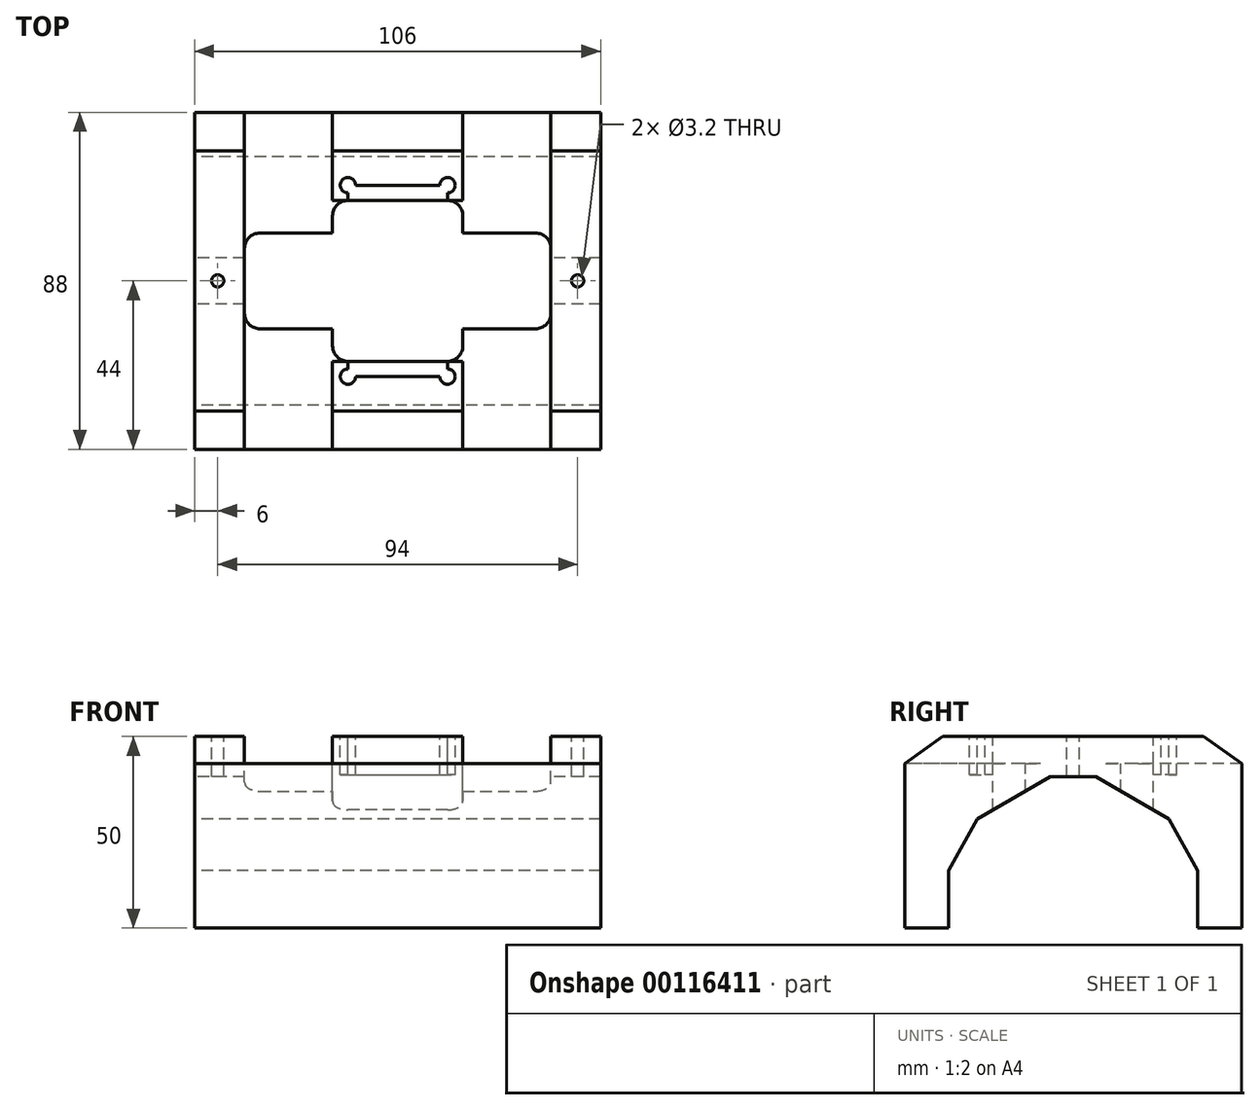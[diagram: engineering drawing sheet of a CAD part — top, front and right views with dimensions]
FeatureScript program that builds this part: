
annotation { "Feature Type Name" : "Feature", "Feature Type Description" : "" }
export const myFeature = defineFeature(function(context is Context, id is Id, definition is map)
    precondition{}
    {
        {
            var Q0;
            Q0=qCreatedBy(makeId("Right.planeOp"),FACE);
            var sketch = newSketch(context, id + "F0", { "sketchPlane" : qUnion([Q0])});
            skLineSegment(sketch, "E0.bottom", {"start": v(-44, 25) * mm, "end": v(44, 25) * mm});
            skLineSegment(sketch, "E0.top", {"start": v(-44, -25) * mm, "end": v(-32.5, -25) * mm});
            skLineSegment(sketch, "E0.left", {"start": v(-44, 25) * mm, "end": v(-44, -25) * mm});
            skLineSegment(sketch, "E0.right", {"start": v(44, 25) * mm, "end": v(44, -25) * mm});
            skPoint(sketch, "E0.middle", {"position": v(0, 0) * mm});
            skLineSegment(sketch, "E1.0", {"start": v(-44, 14.5) * mm, "end": v(44, 14.5) * mm, "construction": true});
            skLineSegment(sketch, "E2.0", {"start": v(-44, 3.5) * mm, "end": v(44, 3.5) * mm, "construction": true});
            skLineSegment(sketch, "E3.0", {"start": v(-44, -10) * mm, "end": v(44, -10) * mm, "construction": true});
            skLineSegment(sketch, "E4", {"start": v(0, -34.88) * mm, "end": v(0, 37.1) * mm, "construction": true});
            skPoint(sketch, "E4.startSnap0", {"position": v(0, -25) * mm});
            skLineSegment(sketch, "E5.0", {"start": v(6, -34.88) * mm, "end": v(6, 37.1) * mm, "construction": true});
            skLineSegment(sketch, "E6.0", {"start": v(25, -34.88) * mm, "end": v(25, 37.1) * mm, "construction": true});
            skLineSegment(sketch, "E7.0", {"start": v(32.5, -34.88) * mm, "end": v(32.5, 37.1) * mm, "construction": true});
            skLineSegment(sketch, "E8", {"start": v(32.5, -10) * mm, "end": v(25, 3.5) * mm});
            skLineSegment(sketch, "E9", {"start": v(25, 3.5) * mm, "end": v(6, 14.5) * mm});
            skLineSegment(sketch, "E10", {"start": v(6, 14.5) * mm, "end": v(0, 14.5) * mm});
            skLineSegment(sketch, "E11", {"start": v(32.5, -10) * mm, "end": v(32.5, -25) * mm});
            skLineSegment(sketch, "E12.MirrorCS", {"start": v(-32.5, -10) * mm, "end": v(-32.5, -25) * mm});
            skLineSegment(sketch, "E13.MirrorCS", {"start": v(-6, 14.5) * mm, "end": v(0, 14.5) * mm});
            skLineSegment(sketch, "E14.MirrorCS", {"start": v(-25, 3.5) * mm, "end": v(-6, 14.5) * mm});
            skLineSegment(sketch, "E15.MirrorCS", {"start": v(-32.5, -10) * mm, "end": v(-25, 3.5) * mm});
            skLineSegment(sketch, "E16.trimOffspring", {"start": v(32.5, -25) * mm, "end": v(44, -25) * mm});
            skSolve(sketch);
        }
        {
            var Q0;
            Q0 = qSketchRegion(id + "F0", true);
            extrude(context, id + "F1", {"entities" : qUnion([Q0]), "endBound" : BoundingType.SYMMETRIC, "depth" : 106 * mm});
        }
        {
            var Q0;
            Q0=makeQuery(id+"F1.opExtrude","SWEPT_FACE",FACE,{"disambiguationData":[OSD([sQuery(id+"F0.wireOp",EDGE,"E0.bottom")])]});
            var sketch = newSketch(context, id + "F2", { "sketchPlane" : qUnion([Q0])});
            skLineSegment(sketch, "E17.0", {"start": v(-53, -44) * mm, "end": v(-53, 44) * mm, "construction": true});
            skLineSegment(sketch, "E18.0", {"start": v(53, -44) * mm, "end": v(53, 44) * mm, "construction": true});
            skLineSegment(sketch, "E19.0", {"start": v(53, 44) * mm, "end": v(-53, 44) * mm, "construction": true});
            skLineSegment(sketch, "E20.0", {"start": v(53, -44) * mm, "end": v(-53, -44) * mm, "construction": true});
            skLineSegment(sketch, "E21.0", {"start": v(-40, -44) * mm, "end": v(-40, 44) * mm, "construction": true});
            skLineSegment(sketch, "E22.0", {"start": v(40, -44) * mm, "end": v(40, 44) * mm, "construction": true});
            skLineSegment(sketch, "E23", {"start": v(-87.37, 0) * mm, "end": v(85.64, 0) * mm, "construction": true});
            skLineSegment(sketch, "E24.0", {"start": v(-87.37, -12.5) * mm, "end": v(85.64, -12.5) * mm, "construction": true});
            skLineSegment(sketch, "E25.bottom", {"start": v(-40, -12.5) * mm, "end": v(40, -12.5) * mm});
            skLineSegment(sketch, "E25.top", {"start": v(-40, 12.5) * mm, "end": v(40, 12.5) * mm});
            skLineSegment(sketch, "E25.left", {"start": v(-40, -12.5) * mm, "end": v(-40, 12.5) * mm});
            skLineSegment(sketch, "E25.right", {"start": v(40, -12.5) * mm, "end": v(40, 12.5) * mm});
            skSolve(sketch);
        }
        {
            var Q0;
            Q0=makeQuery(id+"F2.imprint","IMPRINT",FACE,{"disambiguationData":[TD([[makeQuery(id+"F2.imprint","IMPRINT",EDGE,{"derivedFrom":sQuery(id+"F2.wireOp",EDGE,"E25.bottom")}),1.0]])]});
            extrude(context, id + "F3", {"entities" : qUnion([Q0]), "operationType" : NewBodyOperationType.REMOVE, "oppositeDirection" : true, "depth" : 25 * mm});
        }
        {
            var Q0;
            Q0=makeQuery(id+"F1.opExtrude","SWEPT_FACE",FACE,{"disambiguationData":[OSD([sQuery(id+"F0.wireOp",EDGE,"E0.bottom")])]});
            var sketch = newSketch(context, id + "F4", { "sketchPlane" : qUnion([Q0])});
            skLineSegment(sketch, "E26", {"start": v(0, 82.6) * mm, "end": v(0, -92.17) * mm, "construction": true});
            skLineSegment(sketch, "E27.0", {"start": v(-40, -12.5) * mm, "end": v(-40, 12.5) * mm, "construction": true});
            skLineSegment(sketch, "E28.bottom", {"start": v(-40, 55.24) * mm, "end": v(-17, 55.24) * mm});
            skLineSegment(sketch, "E28.top", {"start": v(-40, -60.7) * mm, "end": v(-17, -60.7) * mm});
            skLineSegment(sketch, "E28.left", {"start": v(-40, 55.24) * mm, "end": v(-40, -60.7) * mm});
            skLineSegment(sketch, "E28.right", {"start": v(-17, 55.24) * mm, "end": v(-17, -60.7) * mm});
            skLineSegment(sketch, "E29.MirrorCS", {"start": v(17, 55.24) * mm, "end": v(17, -60.7) * mm});
            skLineSegment(sketch, "E30.MirrorCS", {"start": v(40, 55.24) * mm, "end": v(40, -60.7) * mm});
            skLineSegment(sketch, "E31.MirrorCS", {"start": v(40, -60.7) * mm, "end": v(17, -60.7) * mm});
            skLineSegment(sketch, "E32.MirrorCS", {"start": v(40, 55.24) * mm, "end": v(17, 55.24) * mm});
            skLineSegment(sketch, "E33.MirrorCS", {"start": v(40, -12.5) * mm, "end": v(40, 12.5) * mm, "construction": true});
            skSolve(sketch);
        }
        {
            var Q0;
            Q0 = qSketchRegion(id + "F4", true);
            extrude(context, id + "F5", {"entities" : qUnion([Q0]), "operationType" : NewBodyOperationType.REMOVE, "oppositeDirection" : true, "depth" : 7 * mm});
        }
        {
            var Q0;
            Q0=makeQuery(id+"F5.boolean.opBoolean","SPLIT",FACE,{"disambiguationData":[TD([makeQuery(id+"F3.boolean.opBoolean","COPY",FACE,{"derivedFrom":makeQuery(id+"F3.opExtrude","SWEPT_FACE",FACE,{"disambiguationData":[OSD([sQuery(id+"F2.wireOp",EDGE,"E25.top")])]})})])],"derivedFrom":makeQuery(id+"F1.opExtrude","SWEPT_FACE",FACE,{"disambiguationData":[OSD([sQuery(id+"F0.wireOp",EDGE,"E0.bottom")])]})});
            var sketch = newSketch(context, id + "F6", { "sketchPlane" : qUnion([Q0])});
            skLineSegment(sketch, "E34.0", {"start": v(-17, 12.5) * mm, "end": v(17, 12.5) * mm, "construction": true});
            skLineSegment(sketch, "E35", {"start": v(-93.94, 0) * mm, "end": v(90.5, 0) * mm, "construction": true});
            skLineSegment(sketch, "E36.0", {"start": v(-93.94, 21) * mm, "end": v(90.5, 21) * mm, "construction": true});
            skLineSegment(sketch, "E37.bottom", {"start": v(-17, 12.5) * mm, "end": v(17, 12.5) * mm});
            skLineSegment(sketch, "E37.top", {"start": v(-17, 21) * mm, "end": v(17, 21) * mm});
            skLineSegment(sketch, "E37.left", {"start": v(-17, 12.5) * mm, "end": v(-17, 21) * mm});
            skLineSegment(sketch, "E37.right", {"start": v(17, 12.5) * mm, "end": v(17, 21) * mm});
            skLineSegment(sketch, "E38.MirrorCS", {"start": v(-17, -12.5) * mm, "end": v(17, -12.5) * mm});
            skLineSegment(sketch, "E39.MirrorCS", {"start": v(17, -12.5) * mm, "end": v(17, -21) * mm});
            skLineSegment(sketch, "E40.MirrorCS", {"start": v(-17, -12.5) * mm, "end": v(-17, -21) * mm});
            skLineSegment(sketch, "E41.MirrorCS", {"start": v(-17, -21) * mm, "end": v(17, -21) * mm});
            skLineSegment(sketch, "E42.MirrorCS", {"start": v(-17, -12.5) * mm, "end": v(17, -12.5) * mm, "construction": true});
            skSolve(sketch);
        }
        {
            var Q0;
            Q0 = qSketchRegion(id + "F6", true);
            extrude(context, id + "F7", {"entities" : qUnion([Q0]), "operationType" : NewBodyOperationType.REMOVE, "endBound" : BoundingType.THROUGH_ALL, "oppositeDirection" : true, "depth" : 25 * mm});
        }
        {
            var Q0;
            Q0=makeQuery(id+"F5.boolean.opBoolean","SPLIT",FACE,{"disambiguationData":[TD([makeQuery(id+"F3.boolean.opBoolean","COPY",FACE,{"derivedFrom":makeQuery(id+"F3.opExtrude","SWEPT_FACE",FACE,{"disambiguationData":[OSD([sQuery(id+"F2.wireOp",EDGE,"E25.top")])]})})])],"derivedFrom":makeQuery(id+"F1.opExtrude","SWEPT_FACE",FACE,{"disambiguationData":[OSD([sQuery(id+"F0.wireOp",EDGE,"E0.bottom")])]})});
            var sketch = newSketch(context, id + "F8", { "sketchPlane" : qUnion([Q0])});
            skLineSegment(sketch, "E43", {"start": v(-72, 0) * mm, "end": v(72, 0) * mm, "construction": true});
            skLineSegment(sketch, "E44", {"start": v(0, 79) * mm, "end": v(0, -53.72) * mm, "construction": true});
            skLineSegment(sketch, "E45.0", {"start": v(-17, 21) * mm, "end": v(17, 21) * mm, "construction": true});
            skLineSegment(sketch, "E46", {"start": v(-61.88, 25) * mm, "end": v(63.54, 25) * mm, "construction": true});
            skLineSegment(sketch, "E47.0", {"start": v(-13, 79) * mm, "end": v(-13, -53.72) * mm});
            skLineSegment(sketch, "E48.0", {"start": v(-17, 44) * mm, "end": v(-17, 21) * mm, "construction": true});
            skLineSegment(sketch, "E49.0", {"start": v(17, 44) * mm, "end": v(17, 21) * mm, "construction": true});
            skLineSegment(sketch, "E50.bottom", {"start": v(-13, 21) * mm, "end": v(13, 21) * mm});
            skLineSegment(sketch, "E50.top", {"start": v(-13, 25) * mm, "end": v(13, 25) * mm});
            skLineSegment(sketch, "E50.left", {"start": v(-13, 21) * mm, "end": v(-13, 25) * mm});
            skLineSegment(sketch, "E50.right", {"start": v(13, 21) * mm, "end": v(13, 25) * mm});
            skLineSegment(sketch, "E51.MirrorCS", {"start": v(-13, -21) * mm, "end": v(-13, -25) * mm});
            skLineSegment(sketch, "E52.MirrorCS", {"start": v(13, -21) * mm, "end": v(13, -25) * mm});
            skLineSegment(sketch, "E53.MirrorCS", {"start": v(-13, -21) * mm, "end": v(13, -21) * mm});
            skLineSegment(sketch, "E54.MirrorCS", {"start": v(-13, -25) * mm, "end": v(13, -25) * mm});
            skLineSegment(sketch, "E55.MirrorCS", {"start": v(-17, -21) * mm, "end": v(17, -21) * mm, "construction": true});
            skSolve(sketch);
        }
        {
            var Q0;
            Q0 = qSketchRegion(id + "F8", true);
            extrude(context, id + "F9", {"entities" : qUnion([Q0]), "operationType" : NewBodyOperationType.REMOVE, "oppositeDirection" : true, "depth" : 10 * mm});
        }
        {
            var Q0;
            Q0=makeQuery(id+"F5.boolean.opBoolean","SPLIT",FACE,{"disambiguationData":[TD([makeQuery(id+"F3.boolean.opBoolean","COPY",FACE,{"derivedFrom":makeQuery(id+"F3.opExtrude","SWEPT_FACE",FACE,{"disambiguationData":[OSD([sQuery(id+"F2.wireOp",EDGE,"E25.top")])]})})])],"derivedFrom":makeQuery(id+"F1.opExtrude","SWEPT_FACE",FACE,{"disambiguationData":[OSD([sQuery(id+"F0.wireOp",EDGE,"E0.bottom")])]})});
            var sketch = newSketch(context, id + "F10", { "sketchPlane" : qUnion([Q0])});
            skLineSegment(sketch, "E56.0", {"start": v(-13, 25) * mm, "end": v(13, 25) * mm, "construction": true});
            skLineSegment(sketch, "E57.0", {"start": v(-13, -25) * mm, "end": v(13, -25) * mm, "construction": true});
            skCircle(sketch, "E58", {"center": v(-13, 25) * mm, "radius": 2 * mm});
            skLineSegment(sketch, "E59", {"start": v(0, 62.34) * mm, "end": v(0, -51.69) * mm, "construction": true});
            skLineSegment(sketch, "E60", {"start": v(-65.66, 0) * mm, "end": v(67.15, 0) * mm, "construction": true});
            skCircle(sketch, "E61.MirrorC", {"center": v(13, 25) * mm, "radius": 2 * mm});
            skCircle(sketch, "E62.MirrorC", {"center": v(-13, -25) * mm, "radius": 2 * mm});
            skCircle(sketch, "E63.MirrorC", {"center": v(13, -25) * mm, "radius": 2 * mm});
            skSolve(sketch);
        }
        {
            var Q0;
            Q0 = qSketchRegion(id + "F10", true);
            extrude(context, id + "F11", {"entities" : qUnion([Q0]), "operationType" : NewBodyOperationType.REMOVE, "oppositeDirection" : true, "depth" : 10 * mm});
        }
        {
            var Q0;
            {var subQ0=sQuery(id+"F0.wireOp",EDGE,"E0.left");var subQ1=sQuery(id+"F0.wireOp",EDGE,"E0.bottom");Q0=makeQuery(id+"F5.boolean.opBoolean","SPLIT",EDGE,{"disambiguationData":[TD([makeQuery(id+"F3.boolean.opBoolean","COPY",FACE,{"derivedFrom":makeQuery(id+"F3.opExtrude","SWEPT_FACE",FACE,{"disambiguationData":[OSD([sQuery(id+"F2.wireOp",EDGE,"E25.left")])]})})])],"derivedFrom":makeQuery(id+"F1.opExtrude","SWEPT_EDGE",EDGE,{"disambiguationData":[OSD([subQ1,subQ0])]})});}
            var Q1;
            {var subQ0=sQuery(id+"F0.wireOp",EDGE,"E0.bottom");var subQ1=sQuery(id+"F0.wireOp",EDGE,"E0.left");Q1=makeQuery(id+"F5.boolean.opBoolean","SPLIT",EDGE,{"disambiguationData":[TD([makeQuery(id+"F5.opExtrude","SWEPT_FACE",FACE,{"disambiguationData":[OSD([sQuery(id+"F4.wireOp",EDGE,"E28.right")])]})])],"derivedFrom":makeQuery(id+"F1.opExtrude","SWEPT_EDGE",EDGE,{"disambiguationData":[OSD([subQ0,subQ1])]})});}
            var Q2;
            {var subQ0=sQuery(id+"F0.wireOp",EDGE,"E0.left");var subQ1=sQuery(id+"F0.wireOp",EDGE,"E0.bottom");Q2=makeQuery(id+"F5.boolean.opBoolean","SPLIT",EDGE,{"disambiguationData":[TD([makeQuery(id+"F3.boolean.opBoolean","COPY",FACE,{"derivedFrom":makeQuery(id+"F3.opExtrude","SWEPT_FACE",FACE,{"disambiguationData":[OSD([sQuery(id+"F2.wireOp",EDGE,"E25.right")])]})})])],"derivedFrom":makeQuery(id+"F1.opExtrude","SWEPT_EDGE",EDGE,{"disambiguationData":[OSD([subQ1,subQ0])]})});}
            chamfer(context, id + "F12", {"entities" : qUnion([Q0, Q1, Q2]), "chamferType" : ChamferType.TWO_OFFSETS, "width1" : 10 * mm, "oppositeDirection" : true, "width2" : 7 * mm, "tangentPropagation" : true});
        }
        {
            var Q0;
            {var subQ0=sQuery(id+"F0.wireOp",EDGE,"E0.right");var subQ1=sQuery(id+"F0.wireOp",EDGE,"E0.bottom");Q0=makeQuery(id+"F5.boolean.opBoolean","SPLIT",EDGE,{"disambiguationData":[TD([makeQuery(id+"F3.boolean.opBoolean","COPY",FACE,{"derivedFrom":makeQuery(id+"F3.opExtrude","SWEPT_FACE",FACE,{"disambiguationData":[OSD([sQuery(id+"F2.wireOp",EDGE,"E25.left")])]})})])],"derivedFrom":makeQuery(id+"F1.opExtrude","SWEPT_EDGE",EDGE,{"disambiguationData":[OSD([subQ1,subQ0])]})});}
            var Q1;
            {var subQ0=sQuery(id+"F0.wireOp",EDGE,"E0.bottom");var subQ1=sQuery(id+"F0.wireOp",EDGE,"E0.right");Q1=makeQuery(id+"F5.boolean.opBoolean","SPLIT",EDGE,{"disambiguationData":[TD([makeQuery(id+"F5.opExtrude","SWEPT_FACE",FACE,{"disambiguationData":[OSD([sQuery(id+"F4.wireOp",EDGE,"E28.right")])]})])],"derivedFrom":makeQuery(id+"F1.opExtrude","SWEPT_EDGE",EDGE,{"disambiguationData":[OSD([subQ0,subQ1])]})});}
            var Q2;
            {var subQ0=sQuery(id+"F0.wireOp",EDGE,"E0.right");var subQ1=sQuery(id+"F0.wireOp",EDGE,"E0.bottom");Q2=makeQuery(id+"F5.boolean.opBoolean","SPLIT",EDGE,{"disambiguationData":[TD([makeQuery(id+"F3.boolean.opBoolean","COPY",FACE,{"derivedFrom":makeQuery(id+"F3.opExtrude","SWEPT_FACE",FACE,{"disambiguationData":[OSD([sQuery(id+"F2.wireOp",EDGE,"E25.right")])]})})])],"derivedFrom":makeQuery(id+"F1.opExtrude","SWEPT_EDGE",EDGE,{"disambiguationData":[OSD([subQ1,subQ0])]})});}
            chamfer(context, id + "F13", {"entities" : qUnion([Q0, Q1, Q2]), "chamferType" : ChamferType.TWO_OFFSETS, "width1" : 10 * mm, "oppositeDirection" : false, "width2" : 7 * mm, "tangentPropagation" : true});
        }
        {
            var Q0;
            {var subQ2=sQuery(id+"F0.wireOp",EDGE,"E0.bottom");Q0=makeQuery(id+"F5.boolean.opBoolean","SPLIT",FACE,{"disambiguationData":[TD([makeQuery(id+"F3.boolean.opBoolean","COPY",FACE,{"derivedFrom":makeQuery(id+"F3.opExtrude","SWEPT_FACE",FACE,{"disambiguationData":[OSD([sQuery(id+"F2.wireOp",EDGE,"E25.left")])]})})])],"derivedFrom":makeQuery(id+"F1.opExtrude","SWEPT_FACE",FACE,{"disambiguationData":[OSD([subQ2])]})});}
            var sketch = newSketch(context, id + "F14", { "sketchPlane" : qUnion([Q0])});
            skLineSegment(sketch, "E64", {"start": v(-75.43, 0) * mm, "end": v(63.16, 0) * mm, "construction": true});
            skLineSegment(sketch, "E65", {"start": v(0, 58.13) * mm, "end": v(0, -55.15) * mm, "construction": true});
            skLineSegment(sketch, "E66.0", {"start": v(-47, 58.13) * mm, "end": v(-47, -55.15) * mm, "construction": true});
            skLineSegment(sketch, "E67.MirrorCS", {"start": v(47, 58.13) * mm, "end": v(47, -55.15) * mm, "construction": true});
            skPoint(sketch, "E68", {"position": v(-47, 0) * mm});
            skPoint(sketch, "E69", {"position": v(47, 0) * mm});
            skSolve(sketch);
        }
        {
            var Q0;
            Q0=sQuery(id+"F14.wireOp",VERTEX,"E68");
            var Q1;
            Q1=sQuery(id+"F14.wireOp",VERTEX,"E69");
            var Q2;
            Q2=makeQuery(id+"F1.opExtrude","SWEPT_BODY",BODY,{"disambiguationData":[OSD([sQuery(id+"F0.wireOp",EDGE,"E0.bottom"),sQuery(id+"F0.wireOp",EDGE,"E0.top"),sQuery(id+"F0.wireOp",EDGE,"E0.left"),sQuery(id+"F0.wireOp",EDGE,"E0.right"),sQuery(id+"F0.wireOp",EDGE,"E8"),sQuery(id+"F0.wireOp",EDGE,"E9"),sQuery(id+"F0.wireOp",EDGE,"E10"),sQuery(id+"F0.wireOp",EDGE,"E11"),sQuery(id+"F0.wireOp",EDGE,"E12.MirrorCS"),sQuery(id+"F0.wireOp",EDGE,"E13.MirrorCS"),sQuery(id+"F0.wireOp",EDGE,"E14.MirrorCS"),sQuery(id+"F0.wireOp",EDGE,"E15.MirrorCS"),sQuery(id+"F0.wireOp",EDGE,"E16.trimOffspring")])]});
            hole(context, id + "F15", {"style" : HoleStyle.SIMPLE, "endStyle" : HoleEndStyle.BLIND, "standardTappedOrClearance" : lookupTablePath({ "standard" : "ISO", "engagement" : "75%", "pitch" : "0.75 mm", "size" : "M4", "type" : "Tapped" }), "standardBlindInLast" : lookupTablePath({ "standard" : "ISO", "engagement" : "75%", "pitch" : "0.75 mm", "size" : "M4", "type" : "Tapped" }), "holeDiameter" : 3.2 * mm, "holeDepth" : 12 * mm, "locations" : qUnion([Q0, Q1]), "scope" : qUnion([Q2])});
        }
        {
            var Q0;
            {var subQ0=sQuery(id+"F6.wireOp",EDGE,"E37.top");var subQ1=sQuery(id+"F4.wireOp",EDGE,"E29.MirrorCS");var subQ7=sQuery(id+"F6.wireOp",EDGE,"E37.right");Q0=makeQuery(id+"F7.boolean.opBoolean","COPY",EDGE,{"disambiguationData":[TD([makeQuery(id+"F1.opExtrude","SWEPT_FACE",FACE,{"disambiguationData":[OSD([sQuery(id+"F0.wireOp",EDGE,"E9")])]})])],"derivedFrom":makeQuery(id+"F7.opExtrude","SWEPT_EDGE",EDGE,{"disambiguationData":[OSD([subQ1,subQ0,subQ7])]})});}
            var Q1;
            {var subQ0=sQuery(id+"F6.wireOp",EDGE,"E37.top");var subQ3=sQuery(id+"F4.wireOp",EDGE,"E28.right");var subQ7=sQuery(id+"F6.wireOp",EDGE,"E37.left");Q1=makeQuery(id+"F7.boolean.opBoolean","COPY",EDGE,{"disambiguationData":[TD([makeQuery(id+"F1.opExtrude","SWEPT_FACE",FACE,{"disambiguationData":[OSD([sQuery(id+"F0.wireOp",EDGE,"E9")])]})])],"derivedFrom":makeQuery(id+"F7.opExtrude","SWEPT_EDGE",EDGE,{"disambiguationData":[OSD([subQ3,subQ0,subQ7])]})});}
            var Q2;
            Q2=makeQuery(id+"F3.boolean.opBoolean","COPY",EDGE,{"derivedFrom":makeQuery(id+"F3.opExtrude","SWEPT_EDGE",EDGE,{"disambiguationData":[OSD([sQuery(id+"F2.wireOp",EDGE,"E25.top"),sQuery(id+"F2.wireOp",EDGE,"E25.left")])]})});
            var Q3;
            Q3=makeQuery(id+"F3.boolean.opBoolean","COPY",EDGE,{"derivedFrom":makeQuery(id+"F3.opExtrude","SWEPT_EDGE",EDGE,{"disambiguationData":[OSD([sQuery(id+"F2.wireOp",EDGE,"E25.bottom"),sQuery(id+"F2.wireOp",EDGE,"E25.left")])]})});
            var Q4;
            {var subQ6=sQuery(id+"F6.wireOp",EDGE,"E40.MirrorCS");var subQ7=sQuery(id+"F6.wireOp",EDGE,"E41.MirrorCS");Q4=makeQuery(id+"F7.boolean.opBoolean","COPY",EDGE,{"disambiguationData":[TD([makeQuery(id+"F1.opExtrude","SWEPT_FACE",FACE,{"disambiguationData":[OSD([sQuery(id+"F0.wireOp",EDGE,"E14.MirrorCS")])]})])],"derivedFrom":makeQuery(id+"F7.opExtrude","SWEPT_EDGE",EDGE,{"disambiguationData":[OSD([subQ6,subQ7])]})});}
            var Q5;
            {var subQ0=sQuery(id+"F6.wireOp",EDGE,"E39.MirrorCS");var subQ7=sQuery(id+"F6.wireOp",EDGE,"E41.MirrorCS");Q5=makeQuery(id+"F7.boolean.opBoolean","COPY",EDGE,{"disambiguationData":[TD([makeQuery(id+"F1.opExtrude","SWEPT_FACE",FACE,{"disambiguationData":[OSD([sQuery(id+"F0.wireOp",EDGE,"E14.MirrorCS")])]})])],"derivedFrom":makeQuery(id+"F7.opExtrude","SWEPT_EDGE",EDGE,{"disambiguationData":[OSD([subQ0,subQ7])]})});}
            var Q6;
            Q6=makeQuery(id+"F3.boolean.opBoolean","COPY",EDGE,{"derivedFrom":makeQuery(id+"F3.opExtrude","SWEPT_EDGE",EDGE,{"disambiguationData":[OSD([sQuery(id+"F2.wireOp",EDGE,"E25.bottom"),sQuery(id+"F2.wireOp",EDGE,"E25.right")])]})});
            var Q7;
            Q7=makeQuery(id+"F3.boolean.opBoolean","COPY",EDGE,{"derivedFrom":makeQuery(id+"F3.opExtrude","SWEPT_EDGE",EDGE,{"disambiguationData":[OSD([sQuery(id+"F2.wireOp",EDGE,"E25.top"),sQuery(id+"F2.wireOp",EDGE,"E25.right")])]})});
            fillet(context, id + "F16", {"entities" : qUnion([Q0, Q1, Q2, Q3, Q4, Q5, Q6, Q7]), "radius" : 4 * mm, "tangentPropagation" : true, "allowEdgeOverflow" : false});
        }
    });
